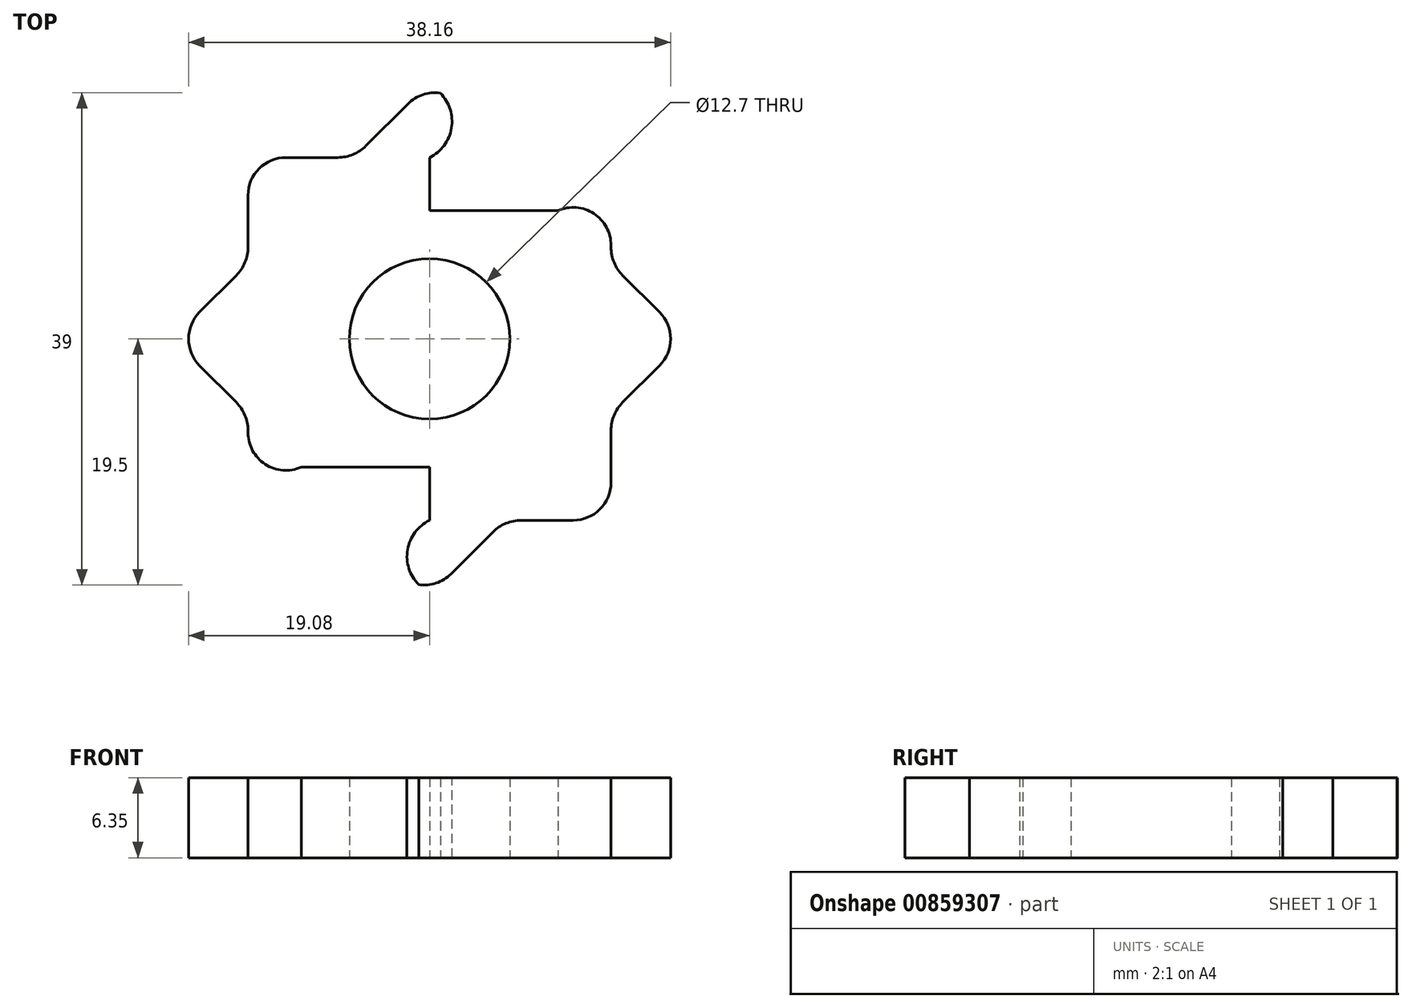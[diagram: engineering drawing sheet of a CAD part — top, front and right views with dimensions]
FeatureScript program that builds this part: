
annotation { "Feature Type Name" : "Feature", "Feature Type Description" : "" }
export const myFeature = defineFeature(function(context is Context, id is Id, definition is map)
    precondition{}
    {
        {
            var Q0;
            Q0=qCreatedBy(makeId("Top.planeOp"),FACE);
            var sketch = newSketch(context, id + "F0", { "sketchPlane" : qUnion([Q0])});
            skCircle(sketch, "E0", {"center": v(0, 0) * mm, "radius": 15 * mm});
            skCircle(sketch, "E1", {"center": v(0, 0) * mm, "radius": 20.32 * mm});
            skCircle(sketch, "E2", {"center": v(0, 0) * mm, "radius": 6.35 * mm});
            skLineSegment(sketch, "E3", {"start": v(0, 0) * mm, "end": v(0, 20.32) * mm});
            skLineSegment(sketch, "E4", {"start": v(0, 0) * mm, "end": v(20.32, 0) * mm});
            skLineSegment(sketch, "E5", {"start": v(0, 0) * mm, "end": v(0, -20.32) * mm});
            skLineSegment(sketch, "E6", {"start": v(0, 0) * mm, "end": v(-20.32, 0) * mm});
            skLineSegment(sketch, "E7", {"start": v(-20.32, 0) * mm, "end": v(0, 20.32) * mm});
            skLineSegment(sketch, "E8", {"start": v(0, 20.32) * mm, "end": v(20.32, 0) * mm});
            skLineSegment(sketch, "E9", {"start": v(20.32, 0) * mm, "end": v(0, -20.32) * mm});
            skLineSegment(sketch, "E10", {"start": v(0, -20.32) * mm, "end": v(-20.32, 0) * mm});
            skLineSegment(sketch, "E11", {"start": v(10.16, -10.16) * mm, "end": v(14.37, -14.37) * mm});
            skLineSegment(sketch, "E12", {"start": v(-10.16, -10.16) * mm, "end": v(-14.37, -14.37) * mm});
            skLineSegment(sketch, "E13", {"start": v(10.16, 10.16) * mm, "end": v(14.37, 14.37) * mm});
            skLineSegment(sketch, "E14", {"start": v(-10.16, 10.16) * mm, "end": v(-14.37, 14.37) * mm});
            skLineSegment(sketch, "E15", {"start": v(10.16, 10.16) * mm, "end": v(10.16, -10.16) * mm});
            skLineSegment(sketch, "E16", {"start": v(10.16, -10.16) * mm, "end": v(-10.16, -10.16) * mm});
            skLineSegment(sketch, "E17", {"start": v(-10.16, -10.16) * mm, "end": v(-10.16, 10.16) * mm});
            skLineSegment(sketch, "E18", {"start": v(-10.16, 10.16) * mm, "end": v(10.16, 10.16) * mm});
            skLineSegment(sketch, "E19", {"start": v(10.16, 0) * mm, "end": v(15, 0) * mm});
            skLineSegment(sketch, "E20", {"start": v(0, 10.16) * mm, "end": v(0, 15) * mm});
            skLineSegment(sketch, "E21", {"start": v(-10.16, 0) * mm, "end": v(-15, 0) * mm});
            skLineSegment(sketch, "E22", {"start": v(0, -10.16) * mm, "end": v(0, -15) * mm});
            skLineSegment(sketch, "E23", {"start": v(0, 0) * mm, "end": v(14.37, 14.37) * mm});
            skLineSegment(sketch, "E24", {"start": v(0, 0) * mm, "end": v(14.37, -14.37) * mm});
            skLineSegment(sketch, "E25", {"start": v(14.37, 14.37) * mm, "end": v(14.37, -14.37) * mm});
            skLineSegment(sketch, "E26", {"start": v(14.37, -14.37) * mm, "end": v(-14.37, -14.37) * mm});
            skLineSegment(sketch, "E27", {"start": v(-14.37, -14.37) * mm, "end": v(-14.37, 14.37) * mm});
            skLineSegment(sketch, "E28", {"start": v(-14.37, 14.37) * mm, "end": v(14.37, 14.37) * mm});
            skSolve(sketch);
        }
        {
            var Q0;
            {var subQ5=sQuery(id+"F0.wireOp",EDGE,"E6");var subQ6=sQuery(id+"F0.wireOp",EDGE,"E2");var subQ7=makeQuery(id+"F0.imprint","INTERSECT",VERTEX,{"derivedFrom":[subQ6,subQ5]});Q0=makeQuery(id+"F0.imprint","IMPRINT",FACE,{"disambiguationData":[TD([[makeQuery(id+"F0.imprint","IMPRINT",EDGE,{"disambiguationData":[TD([[subQ7,-1.0]])],"derivedFrom":subQ6}),-1.0]])]});}
            var Q1;
            {var subQ0=sQuery(id+"F0.wireOp",EDGE,"E24");var subQ1=sQuery(id+"F0.wireOp",EDGE,"E2");var subQ2=makeQuery(id+"F0.imprint","INTERSECT",VERTEX,{"derivedFrom":[subQ1,subQ0]});Q1=makeQuery(id+"F0.imprint","IMPRINT",FACE,{"disambiguationData":[TD([[makeQuery(id+"F0.imprint","IMPRINT",EDGE,{"disambiguationData":[TD([[subQ2,1.0]])],"derivedFrom":subQ1}),-1.0]])]});}
            var Q2;
            {var subQ0=sQuery(id+"F0.wireOp",EDGE,"E24");var subQ1=sQuery(id+"F0.wireOp",EDGE,"E2");var subQ2=makeQuery(id+"F0.imprint","INTERSECT",VERTEX,{"derivedFrom":[subQ1,subQ0]});Q2=makeQuery(id+"F0.imprint","IMPRINT",FACE,{"disambiguationData":[TD([[makeQuery(id+"F0.imprint","IMPRINT",EDGE,{"disambiguationData":[TD([[subQ2,-1.0]])],"derivedFrom":subQ1}),-1.0]])]});}
            var Q3;
            {var subQ0=sQuery(id+"F0.wireOp",EDGE,"E23");var subQ1=sQuery(id+"F0.wireOp",EDGE,"E2");var subQ2=makeQuery(id+"F0.imprint","INTERSECT",VERTEX,{"derivedFrom":[subQ1,subQ0]});Q3=makeQuery(id+"F0.imprint","IMPRINT",FACE,{"disambiguationData":[TD([[makeQuery(id+"F0.imprint","IMPRINT",EDGE,{"disambiguationData":[TD([[subQ2,1.0]])],"derivedFrom":subQ1}),-1.0]])]});}
            var Q4;
            {var subQ5=sQuery(id+"F0.wireOp",EDGE,"E2");var subQ7=sQuery(id+"F0.wireOp",EDGE,"E3");var subQ8=makeQuery(id+"F0.imprint","INTERSECT",VERTEX,{"derivedFrom":[subQ5,subQ7]});Q4=makeQuery(id+"F0.imprint","IMPRINT",FACE,{"disambiguationData":[TD([[makeQuery(id+"F0.imprint","IMPRINT",EDGE,{"disambiguationData":[TD([[subQ8,-1.0]])],"derivedFrom":subQ5}),-1.0]])]});}
            var Q5;
            {var subQ0=sQuery(id+"F0.wireOp",EDGE,"E23");var subQ1=sQuery(id+"F0.wireOp",EDGE,"E2");var subQ2=makeQuery(id+"F0.imprint","INTERSECT",VERTEX,{"derivedFrom":[subQ1,subQ0]});Q5=makeQuery(id+"F0.imprint","IMPRINT",FACE,{"disambiguationData":[TD([[makeQuery(id+"F0.imprint","IMPRINT",EDGE,{"disambiguationData":[TD([[subQ2,-1.0]])],"derivedFrom":subQ1}),-1.0]])]});}
            var Q6;
            {var subQ0=sQuery(id+"F0.wireOp",EDGE,"E7");var subQ1=sQuery(id+"F0.wireOp",EDGE,"E0");var subQ2=makeQuery(id+"F0.imprint","INTERSECT",VERTEX,{"disambiguationData":[OD(0.0)],"derivedFrom":[subQ1,subQ0]});Q6=makeQuery(id+"F0.imprint","IMPRINT",FACE,{"disambiguationData":[TD([[makeQuery(id+"F0.imprint","IMPRINT",EDGE,{"disambiguationData":[TD([[subQ2,1.0]])],"derivedFrom":subQ1}),-1.0]])]});}
            var Q7;
            {var subQ0=sQuery(id+"F0.wireOp",EDGE,"E28");var subQ1=sQuery(id+"F0.wireOp",EDGE,"E0");var subQ2=makeQuery(id+"F0.imprint","INTERSECT",VERTEX,{"disambiguationData":[OD(1.0)],"derivedFrom":[subQ1,subQ0]});Q7=makeQuery(id+"F0.imprint","IMPRINT",FACE,{"disambiguationData":[TD([[makeQuery(id+"F0.imprint","IMPRINT",EDGE,{"disambiguationData":[TD([[subQ2,-1.0]])],"derivedFrom":subQ1}),-1.0]])]});}
            var Q8;
            {var subQ5=sQuery(id+"F0.wireOp",EDGE,"E0");var subQ7=sQuery(id+"F0.wireOp",EDGE,"E28");var subQ9=makeQuery(id+"F0.imprint","INTERSECT",VERTEX,{"disambiguationData":[OD(1.0)],"derivedFrom":[subQ5,subQ7]});Q8=makeQuery(id+"F0.imprint","IMPRINT",FACE,{"disambiguationData":[TD([[makeQuery(id+"F0.imprint","IMPRINT",EDGE,{"disambiguationData":[TD([[subQ9,-1.0]])],"derivedFrom":subQ5}),1.0]])]});}
            var Q9;
            {var subQ0=sQuery(id+"F0.wireOp",EDGE,"E7");var subQ1=sQuery(id+"F0.wireOp",EDGE,"E0");var subQ2=makeQuery(id+"F0.imprint","INTERSECT",VERTEX,{"disambiguationData":[OD(0.0)],"derivedFrom":[subQ1,subQ0]});Q9=makeQuery(id+"F0.imprint","IMPRINT",FACE,{"disambiguationData":[TD([[makeQuery(id+"F0.imprint","IMPRINT",EDGE,{"disambiguationData":[TD([[subQ2,1.0]])],"derivedFrom":subQ1}),1.0]])]});}
            var Q10;
            {var subQ5=sQuery(id+"F0.wireOp",EDGE,"E0");var subQ7=sQuery(id+"F0.wireOp",EDGE,"E28");var subQ9=makeQuery(id+"F0.imprint","INTERSECT",VERTEX,{"disambiguationData":[OD(1.0)],"derivedFrom":[subQ5,subQ7]});Q10=makeQuery(id+"F0.imprint","IMPRINT",FACE,{"disambiguationData":[TD([[makeQuery(id+"F0.imprint","IMPRINT",EDGE,{"disambiguationData":[TD([[subQ9,-1.0]])],"derivedFrom":subQ5}),1.0]])]});}
            var Q11;
            {var subQ0=sQuery(id+"F0.wireOp",EDGE,"E28");var subQ1=sQuery(id+"F0.wireOp",EDGE,"E0");var subQ2=makeQuery(id+"F0.imprint","INTERSECT",VERTEX,{"disambiguationData":[OD(1.0)],"derivedFrom":[subQ1,subQ0]});Q11=makeQuery(id+"F0.imprint","IMPRINT",FACE,{"disambiguationData":[TD([[makeQuery(id+"F0.imprint","IMPRINT",EDGE,{"disambiguationData":[TD([[subQ2,-1.0]])],"derivedFrom":subQ1}),-1.0]])]});}
            var Q12;
            {var subQ0=sQuery(id+"F0.wireOp",EDGE,"E8");var subQ1=sQuery(id+"F0.wireOp",EDGE,"E0");var subQ2=makeQuery(id+"F0.imprint","INTERSECT",VERTEX,{"disambiguationData":[OD(0.0)],"derivedFrom":[subQ1,subQ0]});Q12=makeQuery(id+"F0.imprint","IMPRINT",FACE,{"disambiguationData":[TD([[makeQuery(id+"F0.imprint","IMPRINT",EDGE,{"disambiguationData":[TD([[subQ2,-1.0]])],"derivedFrom":subQ1}),-1.0]])]});}
            var Q13;
            {var subQ1=sQuery(id+"F0.wireOp",EDGE,"E8");var subQ5=sQuery(id+"F0.wireOp",EDGE,"E0");var subQ6=makeQuery(id+"F0.imprint","INTERSECT",VERTEX,{"disambiguationData":[OD(0.0)],"derivedFrom":[subQ5,subQ1]});Q13=makeQuery(id+"F0.imprint","IMPRINT",FACE,{"disambiguationData":[TD([[makeQuery(id+"F0.imprint","IMPRINT",EDGE,{"disambiguationData":[TD([[subQ6,-1.0]])],"derivedFrom":subQ5}),1.0]])]});}
            var Q14;
            {var subQ0=sQuery(id+"F0.wireOp",EDGE,"E28");var subQ1=sQuery(id+"F0.wireOp",EDGE,"E0");var subQ2=makeQuery(id+"F0.imprint","INTERSECT",VERTEX,{"disambiguationData":[OD(1.0)],"derivedFrom":[subQ1,subQ0]});Q14=makeQuery(id+"F0.imprint","IMPRINT",FACE,{"disambiguationData":[TD([[makeQuery(id+"F0.imprint","IMPRINT",EDGE,{"disambiguationData":[TD([[subQ2,-1.0]])],"derivedFrom":subQ1}),-1.0]])]});}
            var Q15;
            {var subQ0=sQuery(id+"F0.wireOp",EDGE,"E7");var subQ1=sQuery(id+"F0.wireOp",EDGE,"E0");var subQ2=makeQuery(id+"F0.imprint","INTERSECT",VERTEX,{"disambiguationData":[OD(0.0)],"derivedFrom":[subQ1,subQ0]});Q15=makeQuery(id+"F0.imprint","IMPRINT",FACE,{"disambiguationData":[TD([[makeQuery(id+"F0.imprint","IMPRINT",EDGE,{"disambiguationData":[TD([[subQ2,-1.0]])],"derivedFrom":subQ1}),-1.0]])]});}
            var Q16;
            {var subQ1=sQuery(id+"F0.wireOp",EDGE,"E7");var subQ6=sQuery(id+"F0.wireOp",EDGE,"E0");var subQ9=makeQuery(id+"F0.imprint","INTERSECT",VERTEX,{"disambiguationData":[OD(0.0)],"derivedFrom":[subQ6,subQ1]});Q16=makeQuery(id+"F0.imprint","IMPRINT",FACE,{"disambiguationData":[TD([[makeQuery(id+"F0.imprint","IMPRINT",EDGE,{"disambiguationData":[TD([[subQ9,-1.0]])],"derivedFrom":subQ6}),1.0]])]});}
            var Q17;
            {var subQ0=sQuery(id+"F0.wireOp",EDGE,"E7");var subQ1=sQuery(id+"F0.wireOp",EDGE,"E0");var subQ2=makeQuery(id+"F0.imprint","INTERSECT",VERTEX,{"disambiguationData":[OD(0.0)],"derivedFrom":[subQ1,subQ0]});Q17=makeQuery(id+"F0.imprint","IMPRINT",FACE,{"disambiguationData":[TD([[makeQuery(id+"F0.imprint","IMPRINT",EDGE,{"disambiguationData":[TD([[subQ2,-1.0]])],"derivedFrom":subQ1}),-1.0]])]});}
            var Q18;
            {var subQ0=sQuery(id+"F0.wireOp",EDGE,"E27");var subQ1=sQuery(id+"F0.wireOp",EDGE,"E0");var subQ2=makeQuery(id+"F0.imprint","INTERSECT",VERTEX,{"disambiguationData":[OD(1.0)],"derivedFrom":[subQ1,subQ0]});Q18=makeQuery(id+"F0.imprint","IMPRINT",FACE,{"disambiguationData":[TD([[makeQuery(id+"F0.imprint","IMPRINT",EDGE,{"disambiguationData":[TD([[subQ2,-1.0]])],"derivedFrom":subQ1}),-1.0]])]});}
            var Q19;
            {var subQ0=sQuery(id+"F0.wireOp",EDGE,"E27");var subQ1=sQuery(id+"F0.wireOp",EDGE,"E0");var subQ2=makeQuery(id+"F0.imprint","INTERSECT",VERTEX,{"disambiguationData":[OD(1.0)],"derivedFrom":[subQ1,subQ0]});Q19=makeQuery(id+"F0.imprint","IMPRINT",FACE,{"disambiguationData":[TD([[makeQuery(id+"F0.imprint","IMPRINT",EDGE,{"disambiguationData":[TD([[subQ2,-1.0]])],"derivedFrom":subQ1}),-1.0]])]});}
            var Q20;
            {var subQ0=sQuery(id+"F0.wireOp",EDGE,"E10");var subQ1=sQuery(id+"F0.wireOp",EDGE,"E0");var subQ2=makeQuery(id+"F0.imprint","INTERSECT",VERTEX,{"disambiguationData":[OD(0.0)],"derivedFrom":[subQ1,subQ0]});Q20=makeQuery(id+"F0.imprint","IMPRINT",FACE,{"disambiguationData":[TD([[makeQuery(id+"F0.imprint","IMPRINT",EDGE,{"disambiguationData":[TD([[subQ2,-1.0]])],"derivedFrom":subQ1}),-1.0]])]});}
            var Q21;
            {var subQ0=sQuery(id+"F0.wireOp",EDGE,"E8");var subQ1=sQuery(id+"F0.wireOp",EDGE,"E0");var subQ2=makeQuery(id+"F0.imprint","INTERSECT",VERTEX,{"disambiguationData":[OD(0.0)],"derivedFrom":[subQ1,subQ0]});Q21=makeQuery(id+"F0.imprint","IMPRINT",FACE,{"disambiguationData":[TD([[makeQuery(id+"F0.imprint","IMPRINT",EDGE,{"disambiguationData":[TD([[subQ2,-1.0]])],"derivedFrom":subQ1}),-1.0]])]});}
            var Q22;
            {var subQ0=sQuery(id+"F0.wireOp",EDGE,"E25");var subQ1=sQuery(id+"F0.wireOp",EDGE,"E0");var subQ2=makeQuery(id+"F0.imprint","INTERSECT",VERTEX,{"disambiguationData":[OD(0.0)],"derivedFrom":[subQ1,subQ0]});Q22=makeQuery(id+"F0.imprint","IMPRINT",FACE,{"disambiguationData":[TD([[makeQuery(id+"F0.imprint","IMPRINT",EDGE,{"disambiguationData":[TD([[subQ2,-1.0]])],"derivedFrom":subQ1}),-1.0]])]});}
            var Q23;
            {var subQ0=sQuery(id+"F0.wireOp",EDGE,"E9");var subQ1=sQuery(id+"F0.wireOp",EDGE,"E0");var subQ2=makeQuery(id+"F0.imprint","INTERSECT",VERTEX,{"disambiguationData":[OD(0.0)],"derivedFrom":[subQ1,subQ0]});Q23=makeQuery(id+"F0.imprint","IMPRINT",FACE,{"disambiguationData":[TD([[makeQuery(id+"F0.imprint","IMPRINT",EDGE,{"disambiguationData":[TD([[subQ2,-1.0]])],"derivedFrom":subQ1}),-1.0]])]});}
            var Q24;
            {var subQ0=sQuery(id+"F0.wireOp",EDGE,"E26");var subQ1=sQuery(id+"F0.wireOp",EDGE,"E0");var subQ2=makeQuery(id+"F0.imprint","INTERSECT",VERTEX,{"disambiguationData":[OD(0.0)],"derivedFrom":[subQ1,subQ0]});Q24=makeQuery(id+"F0.imprint","IMPRINT",FACE,{"disambiguationData":[TD([[makeQuery(id+"F0.imprint","IMPRINT",EDGE,{"disambiguationData":[TD([[subQ2,-1.0]])],"derivedFrom":subQ1}),-1.0]])]});}
            var Q25;
            {var subQ0=sQuery(id+"F0.wireOp",EDGE,"E8");var subQ1=sQuery(id+"F0.wireOp",EDGE,"E0");var subQ2=makeQuery(id+"F0.imprint","INTERSECT",VERTEX,{"disambiguationData":[OD(0.0)],"derivedFrom":[subQ1,subQ0]});Q25=makeQuery(id+"F0.imprint","IMPRINT",FACE,{"disambiguationData":[TD([[makeQuery(id+"F0.imprint","IMPRINT",EDGE,{"disambiguationData":[TD([[subQ2,1.0]])],"derivedFrom":subQ1}),1.0]])]});}
            var Q26;
            {var subQ0=sQuery(id+"F0.wireOp",EDGE,"E8");var subQ1=sQuery(id+"F0.wireOp",EDGE,"E0");var subQ2=makeQuery(id+"F0.imprint","INTERSECT",VERTEX,{"disambiguationData":[OD(0.0)],"derivedFrom":[subQ1,subQ0]});Q26=makeQuery(id+"F0.imprint","IMPRINT",FACE,{"disambiguationData":[TD([[makeQuery(id+"F0.imprint","IMPRINT",EDGE,{"disambiguationData":[TD([[subQ2,1.0]])],"derivedFrom":subQ1}),-1.0]])]});}
            var Q27;
            {var subQ0=sQuery(id+"F0.wireOp",EDGE,"E25");var subQ1=sQuery(id+"F0.wireOp",EDGE,"E0");var subQ2=makeQuery(id+"F0.imprint","INTERSECT",VERTEX,{"disambiguationData":[OD(0.0)],"derivedFrom":[subQ1,subQ0]});Q27=makeQuery(id+"F0.imprint","IMPRINT",FACE,{"disambiguationData":[TD([[makeQuery(id+"F0.imprint","IMPRINT",EDGE,{"disambiguationData":[TD([[subQ2,-1.0]])],"derivedFrom":subQ1}),-1.0]])]});}
            var Q28;
            {var subQ3=sQuery(id+"F0.wireOp",EDGE,"E0");var subQ7=sQuery(id+"F0.wireOp",EDGE,"E25");var subQ9=makeQuery(id+"F0.imprint","INTERSECT",VERTEX,{"disambiguationData":[OD(0.0)],"derivedFrom":[subQ3,subQ7]});Q28=makeQuery(id+"F0.imprint","IMPRINT",FACE,{"disambiguationData":[TD([[makeQuery(id+"F0.imprint","IMPRINT",EDGE,{"disambiguationData":[TD([[subQ9,-1.0]])],"derivedFrom":subQ3}),1.0]])]});}
            var Q29;
            {var subQ3=sQuery(id+"F0.wireOp",EDGE,"E0");var subQ7=sQuery(id+"F0.wireOp",EDGE,"E25");var subQ9=makeQuery(id+"F0.imprint","INTERSECT",VERTEX,{"disambiguationData":[OD(0.0)],"derivedFrom":[subQ3,subQ7]});Q29=makeQuery(id+"F0.imprint","IMPRINT",FACE,{"disambiguationData":[TD([[makeQuery(id+"F0.imprint","IMPRINT",EDGE,{"disambiguationData":[TD([[subQ9,-1.0]])],"derivedFrom":subQ3}),1.0]])]});}
            var Q30;
            {var subQ1=sQuery(id+"F0.wireOp",EDGE,"E9");var subQ7=sQuery(id+"F0.wireOp",EDGE,"E0");var subQ8=makeQuery(id+"F0.imprint","INTERSECT",VERTEX,{"disambiguationData":[OD(0.0)],"derivedFrom":[subQ7,subQ1]});Q30=makeQuery(id+"F0.imprint","IMPRINT",FACE,{"disambiguationData":[TD([[makeQuery(id+"F0.imprint","IMPRINT",EDGE,{"disambiguationData":[TD([[subQ8,-1.0]])],"derivedFrom":subQ7}),1.0]])]});}
            var Q31;
            {var subQ0=sQuery(id+"F0.wireOp",EDGE,"E9");var subQ1=sQuery(id+"F0.wireOp",EDGE,"E0");var subQ2=makeQuery(id+"F0.imprint","INTERSECT",VERTEX,{"disambiguationData":[OD(0.0)],"derivedFrom":[subQ1,subQ0]});Q31=makeQuery(id+"F0.imprint","IMPRINT",FACE,{"disambiguationData":[TD([[makeQuery(id+"F0.imprint","IMPRINT",EDGE,{"disambiguationData":[TD([[subQ2,-1.0]])],"derivedFrom":subQ1}),-1.0]])]});}
            var Q32;
            {var subQ0=sQuery(id+"F0.wireOp",EDGE,"E25");var subQ1=sQuery(id+"F0.wireOp",EDGE,"E0");var subQ2=makeQuery(id+"F0.imprint","INTERSECT",VERTEX,{"disambiguationData":[OD(0.0)],"derivedFrom":[subQ1,subQ0]});Q32=makeQuery(id+"F0.imprint","IMPRINT",FACE,{"disambiguationData":[TD([[makeQuery(id+"F0.imprint","IMPRINT",EDGE,{"disambiguationData":[TD([[subQ2,-1.0]])],"derivedFrom":subQ1}),-1.0]])]});}
            var Q33;
            {var subQ0=sQuery(id+"F0.wireOp",EDGE,"E9");var subQ1=sQuery(id+"F0.wireOp",EDGE,"E0");var subQ2=makeQuery(id+"F0.imprint","INTERSECT",VERTEX,{"disambiguationData":[OD(0.0)],"derivedFrom":[subQ1,subQ0]});Q33=makeQuery(id+"F0.imprint","IMPRINT",FACE,{"disambiguationData":[TD([[makeQuery(id+"F0.imprint","IMPRINT",EDGE,{"disambiguationData":[TD([[subQ2,1.0]])],"derivedFrom":subQ1}),1.0]])]});}
            var Q34;
            {var subQ0=sQuery(id+"F0.wireOp",EDGE,"E9");var subQ1=sQuery(id+"F0.wireOp",EDGE,"E0");var subQ2=makeQuery(id+"F0.imprint","INTERSECT",VERTEX,{"disambiguationData":[OD(0.0)],"derivedFrom":[subQ1,subQ0]});Q34=makeQuery(id+"F0.imprint","IMPRINT",FACE,{"disambiguationData":[TD([[makeQuery(id+"F0.imprint","IMPRINT",EDGE,{"disambiguationData":[TD([[subQ2,1.0]])],"derivedFrom":subQ1}),-1.0]])]});}
            var Q35;
            {var subQ0=sQuery(id+"F0.wireOp",EDGE,"E26");var subQ1=sQuery(id+"F0.wireOp",EDGE,"E0");var subQ2=makeQuery(id+"F0.imprint","INTERSECT",VERTEX,{"disambiguationData":[OD(0.0)],"derivedFrom":[subQ1,subQ0]});Q35=makeQuery(id+"F0.imprint","IMPRINT",FACE,{"disambiguationData":[TD([[makeQuery(id+"F0.imprint","IMPRINT",EDGE,{"disambiguationData":[TD([[subQ2,-1.0]])],"derivedFrom":subQ1}),-1.0]])]});}
            var Q36;
            {var subQ5=sQuery(id+"F0.wireOp",EDGE,"E0");var subQ7=sQuery(id+"F0.wireOp",EDGE,"E26");var subQ9=makeQuery(id+"F0.imprint","INTERSECT",VERTEX,{"disambiguationData":[OD(0.0)],"derivedFrom":[subQ5,subQ7]});Q36=makeQuery(id+"F0.imprint","IMPRINT",FACE,{"disambiguationData":[TD([[makeQuery(id+"F0.imprint","IMPRINT",EDGE,{"disambiguationData":[TD([[subQ9,-1.0]])],"derivedFrom":subQ5}),1.0]])]});}
            var Q37;
            {var subQ5=sQuery(id+"F0.wireOp",EDGE,"E0");var subQ7=sQuery(id+"F0.wireOp",EDGE,"E26");var subQ9=makeQuery(id+"F0.imprint","INTERSECT",VERTEX,{"disambiguationData":[OD(0.0)],"derivedFrom":[subQ5,subQ7]});Q37=makeQuery(id+"F0.imprint","IMPRINT",FACE,{"disambiguationData":[TD([[makeQuery(id+"F0.imprint","IMPRINT",EDGE,{"disambiguationData":[TD([[subQ9,-1.0]])],"derivedFrom":subQ5}),1.0]])]});}
            var Q38;
            {var subQ3=sQuery(id+"F0.wireOp",EDGE,"E10");var subQ5=sQuery(id+"F0.wireOp",EDGE,"E0");var subQ6=makeQuery(id+"F0.imprint","INTERSECT",VERTEX,{"disambiguationData":[OD(0.0)],"derivedFrom":[subQ5,subQ3]});Q38=makeQuery(id+"F0.imprint","IMPRINT",FACE,{"disambiguationData":[TD([[makeQuery(id+"F0.imprint","IMPRINT",EDGE,{"disambiguationData":[TD([[subQ6,-1.0]])],"derivedFrom":subQ5}),1.0]])]});}
            var Q39;
            {var subQ0=sQuery(id+"F0.wireOp",EDGE,"E10");var subQ1=sQuery(id+"F0.wireOp",EDGE,"E0");var subQ2=makeQuery(id+"F0.imprint","INTERSECT",VERTEX,{"disambiguationData":[OD(0.0)],"derivedFrom":[subQ1,subQ0]});Q39=makeQuery(id+"F0.imprint","IMPRINT",FACE,{"disambiguationData":[TD([[makeQuery(id+"F0.imprint","IMPRINT",EDGE,{"disambiguationData":[TD([[subQ2,-1.0]])],"derivedFrom":subQ1}),-1.0]])]});}
            var Q40;
            {var subQ0=sQuery(id+"F0.wireOp",EDGE,"E26");var subQ1=sQuery(id+"F0.wireOp",EDGE,"E0");var subQ2=makeQuery(id+"F0.imprint","INTERSECT",VERTEX,{"disambiguationData":[OD(0.0)],"derivedFrom":[subQ1,subQ0]});Q40=makeQuery(id+"F0.imprint","IMPRINT",FACE,{"disambiguationData":[TD([[makeQuery(id+"F0.imprint","IMPRINT",EDGE,{"disambiguationData":[TD([[subQ2,-1.0]])],"derivedFrom":subQ1}),-1.0]])]});}
            var Q41;
            {var subQ0=sQuery(id+"F0.wireOp",EDGE,"E10");var subQ1=sQuery(id+"F0.wireOp",EDGE,"E0");var subQ2=makeQuery(id+"F0.imprint","INTERSECT",VERTEX,{"disambiguationData":[OD(0.0)],"derivedFrom":[subQ1,subQ0]});Q41=makeQuery(id+"F0.imprint","IMPRINT",FACE,{"disambiguationData":[TD([[makeQuery(id+"F0.imprint","IMPRINT",EDGE,{"disambiguationData":[TD([[subQ2,1.0]])],"derivedFrom":subQ1}),1.0]])]});}
            var Q42;
            {var subQ0=sQuery(id+"F0.wireOp",EDGE,"E27");var subQ1=sQuery(id+"F0.wireOp",EDGE,"E0");var subQ2=makeQuery(id+"F0.imprint","INTERSECT",VERTEX,{"disambiguationData":[OD(1.0)],"derivedFrom":[subQ1,subQ0]});Q42=makeQuery(id+"F0.imprint","IMPRINT",FACE,{"disambiguationData":[TD([[makeQuery(id+"F0.imprint","IMPRINT",EDGE,{"disambiguationData":[TD([[subQ2,-1.0]])],"derivedFrom":subQ1}),-1.0]])]});}
            var Q43;
            {var subQ0=sQuery(id+"F0.wireOp",EDGE,"E10");var subQ1=sQuery(id+"F0.wireOp",EDGE,"E0");var subQ2=makeQuery(id+"F0.imprint","INTERSECT",VERTEX,{"disambiguationData":[OD(0.0)],"derivedFrom":[subQ1,subQ0]});Q43=makeQuery(id+"F0.imprint","IMPRINT",FACE,{"disambiguationData":[TD([[makeQuery(id+"F0.imprint","IMPRINT",EDGE,{"disambiguationData":[TD([[subQ2,1.0]])],"derivedFrom":subQ1}),-1.0]])]});}
            var Q44;
            {var subQ0=sQuery(id+"F0.wireOp",EDGE,"E14");var subQ1=sQuery(id+"F0.wireOp",EDGE,"E0");var subQ2=makeQuery(id+"F0.imprint","INTERSECT",VERTEX,{"derivedFrom":[subQ1,subQ0]});Q44=makeQuery(id+"F0.imprint","IMPRINT",FACE,{"disambiguationData":[TD([[makeQuery(id+"F0.imprint","IMPRINT",EDGE,{"disambiguationData":[TD([[subQ2,1.0]])],"derivedFrom":subQ1}),1.0]])]});}
            var Q45;
            {var subQ0=sQuery(id+"F0.wireOp",EDGE,"E14");var subQ1=sQuery(id+"F0.wireOp",EDGE,"E0");var subQ2=makeQuery(id+"F0.imprint","INTERSECT",VERTEX,{"derivedFrom":[subQ1,subQ0]});Q45=makeQuery(id+"F0.imprint","IMPRINT",FACE,{"disambiguationData":[TD([[makeQuery(id+"F0.imprint","IMPRINT",EDGE,{"disambiguationData":[TD([[subQ2,1.0]])],"derivedFrom":subQ1}),-1.0]])]});}
            var Q46;
            {var subQ0=sQuery(id+"F0.wireOp",EDGE,"E3");var subQ1=sQuery(id+"F0.wireOp",EDGE,"E0");var subQ2=makeQuery(id+"F0.imprint","INTERSECT",VERTEX,{"derivedFrom":[subQ1,subQ0]});Q46=makeQuery(id+"F0.imprint","IMPRINT",FACE,{"disambiguationData":[TD([[makeQuery(id+"F0.imprint","IMPRINT",EDGE,{"disambiguationData":[TD([[subQ2,-1.0]])],"derivedFrom":subQ1}),1.0]])]});}
            var Q47;
            {var subQ0=sQuery(id+"F0.wireOp",EDGE,"E3");var subQ1=sQuery(id+"F0.wireOp",EDGE,"E0");var subQ2=makeQuery(id+"F0.imprint","INTERSECT",VERTEX,{"derivedFrom":[subQ1,subQ0]});Q47=makeQuery(id+"F0.imprint","IMPRINT",FACE,{"disambiguationData":[TD([[makeQuery(id+"F0.imprint","IMPRINT",EDGE,{"disambiguationData":[TD([[subQ2,1.0]])],"derivedFrom":subQ1}),-1.0]])]});}
            var Q48;
            {var subQ0=sQuery(id+"F0.wireOp",EDGE,"E3");var subQ1=sQuery(id+"F0.wireOp",EDGE,"E0");var subQ2=makeQuery(id+"F0.imprint","INTERSECT",VERTEX,{"derivedFrom":[subQ1,subQ0]});Q48=makeQuery(id+"F0.imprint","IMPRINT",FACE,{"disambiguationData":[TD([[makeQuery(id+"F0.imprint","IMPRINT",EDGE,{"disambiguationData":[TD([[subQ2,1.0]])],"derivedFrom":subQ1}),1.0]])]});}
            var Q49;
            {var subQ0=sQuery(id+"F0.wireOp",EDGE,"E3");var subQ1=sQuery(id+"F0.wireOp",EDGE,"E0");var subQ2=makeQuery(id+"F0.imprint","INTERSECT",VERTEX,{"derivedFrom":[subQ1,subQ0]});Q49=makeQuery(id+"F0.imprint","IMPRINT",FACE,{"disambiguationData":[TD([[makeQuery(id+"F0.imprint","IMPRINT",EDGE,{"disambiguationData":[TD([[subQ2,-1.0]])],"derivedFrom":subQ1}),-1.0]])]});}
            var Q50;
            {var subQ0=sQuery(id+"F0.wireOp",EDGE,"E13");var subQ1=sQuery(id+"F0.wireOp",EDGE,"E0");var subQ2=makeQuery(id+"F0.imprint","INTERSECT",VERTEX,{"derivedFrom":[subQ1,subQ0]});Q50=makeQuery(id+"F0.imprint","IMPRINT",FACE,{"disambiguationData":[TD([[makeQuery(id+"F0.imprint","IMPRINT",EDGE,{"disambiguationData":[TD([[subQ2,1.0]])],"derivedFrom":subQ1}),1.0]])]});}
            var Q51;
            {var subQ0=sQuery(id+"F0.wireOp",EDGE,"E13");var subQ1=sQuery(id+"F0.wireOp",EDGE,"E0");var subQ2=makeQuery(id+"F0.imprint","INTERSECT",VERTEX,{"derivedFrom":[subQ1,subQ0]});Q51=makeQuery(id+"F0.imprint","IMPRINT",FACE,{"disambiguationData":[TD([[makeQuery(id+"F0.imprint","IMPRINT",EDGE,{"disambiguationData":[TD([[subQ2,1.0]])],"derivedFrom":subQ1}),-1.0]])]});}
            var Q52;
            {var subQ0=sQuery(id+"F0.wireOp",EDGE,"E4");var subQ1=sQuery(id+"F0.wireOp",EDGE,"E0");var subQ2=makeQuery(id+"F0.imprint","INTERSECT",VERTEX,{"derivedFrom":[subQ1,subQ0]});Q52=makeQuery(id+"F0.imprint","IMPRINT",FACE,{"disambiguationData":[TD([[makeQuery(id+"F0.imprint","IMPRINT",EDGE,{"disambiguationData":[TD([[subQ2,-1.0]])],"derivedFrom":subQ1}),1.0]])]});}
            var Q53;
            {var subQ0=sQuery(id+"F0.wireOp",EDGE,"E4");var subQ1=sQuery(id+"F0.wireOp",EDGE,"E0");var subQ2=makeQuery(id+"F0.imprint","INTERSECT",VERTEX,{"derivedFrom":[subQ1,subQ0]});Q53=makeQuery(id+"F0.imprint","IMPRINT",FACE,{"disambiguationData":[TD([[makeQuery(id+"F0.imprint","IMPRINT",EDGE,{"disambiguationData":[TD([[subQ2,1.0]])],"derivedFrom":subQ1}),1.0]])]});}
            var Q54;
            {var subQ0=sQuery(id+"F0.wireOp",EDGE,"E4");var subQ1=sQuery(id+"F0.wireOp",EDGE,"E0");var subQ2=makeQuery(id+"F0.imprint","INTERSECT",VERTEX,{"derivedFrom":[subQ1,subQ0]});Q54=makeQuery(id+"F0.imprint","IMPRINT",FACE,{"disambiguationData":[TD([[makeQuery(id+"F0.imprint","IMPRINT",EDGE,{"disambiguationData":[TD([[subQ2,1.0]])],"derivedFrom":subQ1}),-1.0]])]});}
            var Q55;
            {var subQ0=sQuery(id+"F0.wireOp",EDGE,"E4");var subQ1=sQuery(id+"F0.wireOp",EDGE,"E0");var subQ2=makeQuery(id+"F0.imprint","INTERSECT",VERTEX,{"derivedFrom":[subQ1,subQ0]});Q55=makeQuery(id+"F0.imprint","IMPRINT",FACE,{"disambiguationData":[TD([[makeQuery(id+"F0.imprint","IMPRINT",EDGE,{"disambiguationData":[TD([[subQ2,-1.0]])],"derivedFrom":subQ1}),-1.0]])]});}
            var Q56;
            {var subQ0=sQuery(id+"F0.wireOp",EDGE,"E11");var subQ1=sQuery(id+"F0.wireOp",EDGE,"E0");var subQ2=makeQuery(id+"F0.imprint","INTERSECT",VERTEX,{"derivedFrom":[subQ1,subQ0]});Q56=makeQuery(id+"F0.imprint","IMPRINT",FACE,{"disambiguationData":[TD([[makeQuery(id+"F0.imprint","IMPRINT",EDGE,{"disambiguationData":[TD([[subQ2,1.0]])],"derivedFrom":subQ1}),1.0]])]});}
            var Q57;
            {var subQ0=sQuery(id+"F0.wireOp",EDGE,"E11");var subQ1=sQuery(id+"F0.wireOp",EDGE,"E0");var subQ2=makeQuery(id+"F0.imprint","INTERSECT",VERTEX,{"derivedFrom":[subQ1,subQ0]});Q57=makeQuery(id+"F0.imprint","IMPRINT",FACE,{"disambiguationData":[TD([[makeQuery(id+"F0.imprint","IMPRINT",EDGE,{"disambiguationData":[TD([[subQ2,1.0]])],"derivedFrom":subQ1}),-1.0]])]});}
            var Q58;
            {var subQ0=sQuery(id+"F0.wireOp",EDGE,"E5");var subQ1=sQuery(id+"F0.wireOp",EDGE,"E0");var subQ2=makeQuery(id+"F0.imprint","INTERSECT",VERTEX,{"derivedFrom":[subQ1,subQ0]});Q58=makeQuery(id+"F0.imprint","IMPRINT",FACE,{"disambiguationData":[TD([[makeQuery(id+"F0.imprint","IMPRINT",EDGE,{"disambiguationData":[TD([[subQ2,-1.0]])],"derivedFrom":subQ1}),1.0]])]});}
            var Q59;
            {var subQ0=sQuery(id+"F0.wireOp",EDGE,"E5");var subQ1=sQuery(id+"F0.wireOp",EDGE,"E0");var subQ2=makeQuery(id+"F0.imprint","INTERSECT",VERTEX,{"derivedFrom":[subQ1,subQ0]});Q59=makeQuery(id+"F0.imprint","IMPRINT",FACE,{"disambiguationData":[TD([[makeQuery(id+"F0.imprint","IMPRINT",EDGE,{"disambiguationData":[TD([[subQ2,1.0]])],"derivedFrom":subQ1}),1.0]])]});}
            var Q60;
            {var subQ0=sQuery(id+"F0.wireOp",EDGE,"E5");var subQ1=sQuery(id+"F0.wireOp",EDGE,"E0");var subQ2=makeQuery(id+"F0.imprint","INTERSECT",VERTEX,{"derivedFrom":[subQ1,subQ0]});Q60=makeQuery(id+"F0.imprint","IMPRINT",FACE,{"disambiguationData":[TD([[makeQuery(id+"F0.imprint","IMPRINT",EDGE,{"disambiguationData":[TD([[subQ2,1.0]])],"derivedFrom":subQ1}),-1.0]])]});}
            var Q61;
            {var subQ0=sQuery(id+"F0.wireOp",EDGE,"E5");var subQ1=sQuery(id+"F0.wireOp",EDGE,"E0");var subQ2=makeQuery(id+"F0.imprint","INTERSECT",VERTEX,{"derivedFrom":[subQ1,subQ0]});Q61=makeQuery(id+"F0.imprint","IMPRINT",FACE,{"disambiguationData":[TD([[makeQuery(id+"F0.imprint","IMPRINT",EDGE,{"disambiguationData":[TD([[subQ2,-1.0]])],"derivedFrom":subQ1}),-1.0]])]});}
            var Q62;
            {var subQ0=sQuery(id+"F0.wireOp",EDGE,"E12");var subQ1=sQuery(id+"F0.wireOp",EDGE,"E0");var subQ2=makeQuery(id+"F0.imprint","INTERSECT",VERTEX,{"derivedFrom":[subQ1,subQ0]});Q62=makeQuery(id+"F0.imprint","IMPRINT",FACE,{"disambiguationData":[TD([[makeQuery(id+"F0.imprint","IMPRINT",EDGE,{"disambiguationData":[TD([[subQ2,1.0]])],"derivedFrom":subQ1}),1.0]])]});}
            var Q63;
            {var subQ0=sQuery(id+"F0.wireOp",EDGE,"E12");var subQ1=sQuery(id+"F0.wireOp",EDGE,"E0");var subQ2=makeQuery(id+"F0.imprint","INTERSECT",VERTEX,{"derivedFrom":[subQ1,subQ0]});Q63=makeQuery(id+"F0.imprint","IMPRINT",FACE,{"disambiguationData":[TD([[makeQuery(id+"F0.imprint","IMPRINT",EDGE,{"disambiguationData":[TD([[subQ2,1.0]])],"derivedFrom":subQ1}),-1.0]])]});}
            var Q64;
            {var subQ0=sQuery(id+"F0.wireOp",EDGE,"E6");var subQ1=sQuery(id+"F0.wireOp",EDGE,"E0");var subQ2=makeQuery(id+"F0.imprint","INTERSECT",VERTEX,{"derivedFrom":[subQ1,subQ0]});Q64=makeQuery(id+"F0.imprint","IMPRINT",FACE,{"disambiguationData":[TD([[makeQuery(id+"F0.imprint","IMPRINT",EDGE,{"disambiguationData":[TD([[subQ2,-1.0]])],"derivedFrom":subQ1}),1.0]])]});}
            var Q65;
            {var subQ5=sQuery(id+"F0.wireOp",EDGE,"E27");var subQ6=sQuery(id+"F0.wireOp",EDGE,"E0");var subQ7=makeQuery(id+"F0.imprint","INTERSECT",VERTEX,{"disambiguationData":[OD(1.0)],"derivedFrom":[subQ6,subQ5]});Q65=makeQuery(id+"F0.imprint","IMPRINT",FACE,{"disambiguationData":[TD([[makeQuery(id+"F0.imprint","IMPRINT",EDGE,{"disambiguationData":[TD([[subQ7,-1.0]])],"derivedFrom":subQ6}),1.0]])]});}
            var Q66;
            {var subQ0=sQuery(id+"F0.wireOp",EDGE,"E6");var subQ1=sQuery(id+"F0.wireOp",EDGE,"E0");var subQ2=makeQuery(id+"F0.imprint","INTERSECT",VERTEX,{"derivedFrom":[subQ1,subQ0]});Q66=makeQuery(id+"F0.imprint","IMPRINT",FACE,{"disambiguationData":[TD([[makeQuery(id+"F0.imprint","IMPRINT",EDGE,{"disambiguationData":[TD([[subQ2,-1.0]])],"derivedFrom":subQ1}),-1.0]])]});}
            var Q67;
            {var subQ0=sQuery(id+"F0.wireOp",EDGE,"E6");var subQ1=sQuery(id+"F0.wireOp",EDGE,"E0");var subQ2=makeQuery(id+"F0.imprint","INTERSECT",VERTEX,{"derivedFrom":[subQ1,subQ0]});Q67=makeQuery(id+"F0.imprint","IMPRINT",FACE,{"disambiguationData":[TD([[makeQuery(id+"F0.imprint","IMPRINT",EDGE,{"disambiguationData":[TD([[subQ2,1.0]])],"derivedFrom":subQ1}),-1.0]])]});}
            var Q68;
            {var subQ0=sQuery(id+"F0.wireOp",EDGE,"E6");var subQ1=sQuery(id+"F0.wireOp",EDGE,"E0");var subQ2=makeQuery(id+"F0.imprint","INTERSECT",VERTEX,{"derivedFrom":[subQ1,subQ0]});Q68=makeQuery(id+"F0.imprint","IMPRINT",FACE,{"disambiguationData":[TD([[makeQuery(id+"F0.imprint","IMPRINT",EDGE,{"disambiguationData":[TD([[subQ2,1.0]])],"derivedFrom":subQ1}),1.0]])]});}
            extrude(context, id + "F1", {"entities" : qUnion([Q0, Q1, Q2, Q3, Q4, Q5, Q6, Q7, Q8, Q9, Q10, Q11, Q12, Q13, Q14, Q15, Q16, Q17, Q18, Q19, Q20, Q21, Q22, Q23, Q24, Q25, Q26, Q27, Q28, Q29, Q30, Q31, Q32, Q33, Q34, Q35, Q36, Q37, Q38, Q39, Q40, Q41, Q42, Q43, Q44, Q45, Q46, Q47, Q48, Q49, Q50, Q51, Q52, Q53, Q54, Q55, Q56, Q57, Q58, Q59, Q60, Q61, Q62, Q63, Q64, Q65, Q66, Q67, Q68]), "depth" : 6.35 * mm, "offsetDistance" : 25.4 * mm});
        }
        {
            var Q0;
            Q0=makeQuery(id+"F1.opExtrude","SWEPT_EDGE",EDGE,{"disambiguationData":[OSD([sQuery(id+"F0.wireOp",EDGE,"E10"),sQuery(id+"F0.wireOp",EDGE,"E26")])]});
            var Q1;
            Q1=makeQuery(id+"F1.opExtrude","SWEPT_EDGE",EDGE,{"disambiguationData":[OSD([sQuery(id+"F0.wireOp",EDGE,"E9"),sQuery(id+"F0.wireOp",EDGE,"E26")])]});
            var Q2;
            Q2=makeQuery(id+"F1.opExtrude","SWEPT_EDGE",EDGE,{"disambiguationData":[OSD([sQuery(id+"F0.wireOp",EDGE,"E7"),sQuery(id+"F0.wireOp",EDGE,"E28")])]});
            var Q3;
            Q3=makeQuery(id+"F1.opExtrude","SWEPT_EDGE",EDGE,{"disambiguationData":[OSD([sQuery(id+"F0.wireOp",EDGE,"E8"),sQuery(id+"F0.wireOp",EDGE,"E28")])]});
            var Q4;
            Q4=makeQuery(id+"F1.opExtrude","SWEPT_EDGE",EDGE,{"disambiguationData":[OSD([sQuery(id+"F0.wireOp",EDGE,"E8"),sQuery(id+"F0.wireOp",EDGE,"E25")])]});
            var Q5;
            Q5=makeQuery(id+"F1.opExtrude","SWEPT_EDGE",EDGE,{"disambiguationData":[OSD([sQuery(id+"F0.wireOp",EDGE,"E9"),sQuery(id+"F0.wireOp",EDGE,"E25")])]});
            var Q6;
            Q6=makeQuery(id+"F1.opExtrude","SWEPT_EDGE",EDGE,{"disambiguationData":[OSD([sQuery(id+"F0.wireOp",EDGE,"E7"),sQuery(id+"F0.wireOp",EDGE,"E27")])]});
            var Q7;
            Q7=makeQuery(id+"F1.opExtrude","SWEPT_EDGE",EDGE,{"disambiguationData":[OSD([sQuery(id+"F0.wireOp",EDGE,"E10"),sQuery(id+"F0.wireOp",EDGE,"E27")])]});
            fillet(context, id + "F2", {"entities" : qUnion([Q0, Q1, Q2, Q3, Q4, Q5, Q6, Q7]), "radius" : 3.17 * mm, "tangentPropagation" : true, "allowEdgeOverflow" : false});
        }
        {
            var Q0;
            Q0=makeQuery(id+"F1.opExtrude","SWEPT_EDGE",EDGE,{"disambiguationData":[OSD([sQuery(id+"F0.wireOp",EDGE,"E1"),sQuery(id+"F0.wireOp",EDGE,"E14"),sQuery(id+"F0.wireOp",EDGE,"E27"),sQuery(id+"F0.wireOp",EDGE,"E28")])]});
            var Q1;
            Q1=makeQuery(id+"F1.opExtrude","SWEPT_EDGE",EDGE,{"disambiguationData":[OSD([sQuery(id+"F0.wireOp",EDGE,"E1"),sQuery(id+"F0.wireOp",EDGE,"E6"),sQuery(id+"F0.wireOp",EDGE,"E7"),sQuery(id+"F0.wireOp",EDGE,"E10")])]});
            var Q2;
            Q2=makeQuery(id+"F1.opExtrude","SWEPT_EDGE",EDGE,{"disambiguationData":[OSD([sQuery(id+"F0.wireOp",EDGE,"E1"),sQuery(id+"F0.wireOp",EDGE,"E12"),sQuery(id+"F0.wireOp",EDGE,"E26"),sQuery(id+"F0.wireOp",EDGE,"E27")])]});
            var Q3;
            Q3=makeQuery(id+"F1.opExtrude","SWEPT_EDGE",EDGE,{"disambiguationData":[OSD([sQuery(id+"F0.wireOp",EDGE,"E1"),sQuery(id+"F0.wireOp",EDGE,"E3"),sQuery(id+"F0.wireOp",EDGE,"E7"),sQuery(id+"F0.wireOp",EDGE,"E8")])]});
            var Q4;
            Q4=makeQuery(id+"F1.opExtrude","SWEPT_EDGE",EDGE,{"disambiguationData":[OSD([sQuery(id+"F0.wireOp",EDGE,"E1"),sQuery(id+"F0.wireOp",EDGE,"E5"),sQuery(id+"F0.wireOp",EDGE,"E9"),sQuery(id+"F0.wireOp",EDGE,"E10")])]});
            var Q5;
            Q5=makeQuery(id+"F1.opExtrude","SWEPT_EDGE",EDGE,{"disambiguationData":[OSD([sQuery(id+"F0.wireOp",EDGE,"E1"),sQuery(id+"F0.wireOp",EDGE,"E13"),sQuery(id+"F0.wireOp",EDGE,"E25"),sQuery(id+"F0.wireOp",EDGE,"E28")])]});
            var Q6;
            Q6=makeQuery(id+"F1.opExtrude","SWEPT_EDGE",EDGE,{"disambiguationData":[OSD([sQuery(id+"F0.wireOp",EDGE,"E1"),sQuery(id+"F0.wireOp",EDGE,"E4"),sQuery(id+"F0.wireOp",EDGE,"E8"),sQuery(id+"F0.wireOp",EDGE,"E9")])]});
            var Q7;
            Q7=makeQuery(id+"F1.opExtrude","SWEPT_EDGE",EDGE,{"disambiguationData":[OSD([sQuery(id+"F0.wireOp",EDGE,"E1"),sQuery(id+"F0.wireOp",EDGE,"E11"),sQuery(id+"F0.wireOp",EDGE,"E25"),sQuery(id+"F0.wireOp",EDGE,"E26")])]});
            fillet(context, id + "F3", {"entities" : qUnion([Q0, Q1, Q2, Q3, Q4, Q5, Q6, Q7]), "radius" : 3 * mm, "tangentPropagation" : true, "allowEdgeOverflow" : false});
        }
    });
